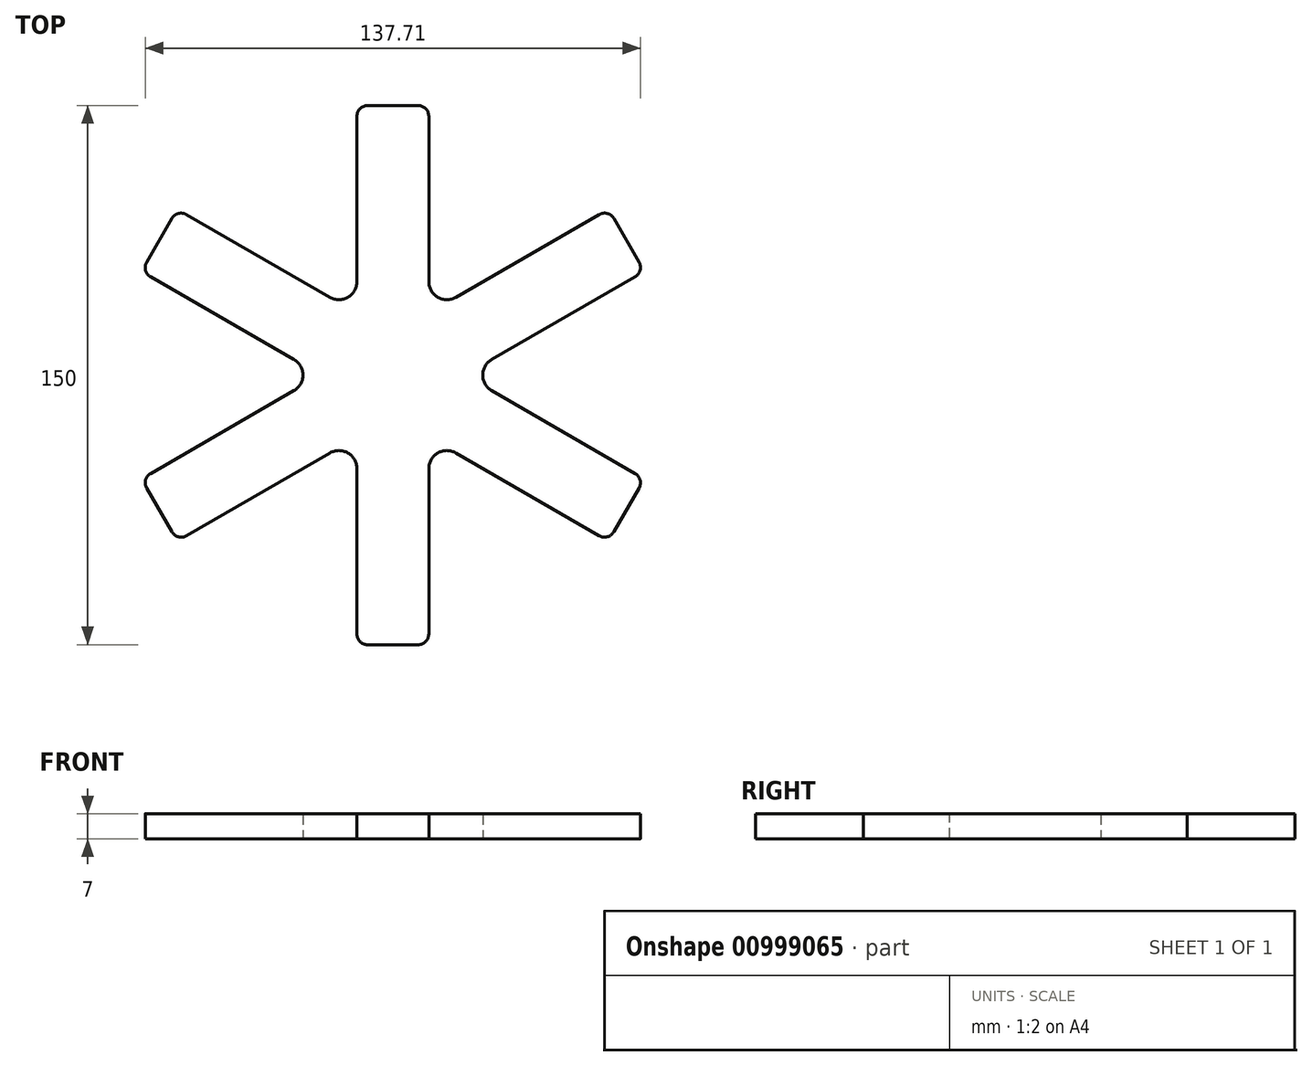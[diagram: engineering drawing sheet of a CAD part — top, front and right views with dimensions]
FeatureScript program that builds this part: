
annotation { "Feature Type Name" : "Feature", "Feature Type Description" : "" }
export const myFeature = defineFeature(function(context is Context, id is Id, definition is map)
    precondition{}
    {
        {
            var Q0;
            Q0=qCreatedBy(makeId("Top.planeOp"),FACE);
            var sketch = newSketch(context, id + "F0", { "sketchPlane" : qUnion([Q0])});
            skLineSegment(sketch, "E0.bottom", {"start": v(-35.4, 96) * mm, "end": v(-15.4, 96) * mm});
            skLineSegment(sketch, "E0.top", {"start": v(-35.4, -54) * mm, "end": v(-15.4, -54) * mm});
            skLineSegment(sketch, "E0.left", {"start": v(-35.4, 96) * mm, "end": v(-35.4, 38.31) * mm});
            skLineSegment(sketch, "E0.right", {"start": v(-15.4, 96) * mm, "end": v(-15.4, 38.31) * mm});
            skLineSegment(sketch, "E1.1.0", {"start": v(44.54, 49.83) * mm, "end": v(-5.4, 21) * mm});
            skLineSegment(sketch, "E1.1.1", {"start": v(34.54, 67.15) * mm, "end": v(44.54, 49.83) * mm});
            skLineSegment(sketch, "E1.1.2", {"start": v(34.54, 67.15) * mm, "end": v(-15.4, 38.31) * mm});
            skLineSegment(sketch, "E1.1.3", {"start": v(-95.36, -7.85) * mm, "end": v(-85.36, -25.17) * mm});
            skLineSegment(sketch, "E1.2.0", {"start": v(34.54, -25.17) * mm, "end": v(-15.4, 3.67) * mm});
            skLineSegment(sketch, "E1.2.1", {"start": v(44.54, -7.85) * mm, "end": v(34.54, -25.17) * mm});
            skLineSegment(sketch, "E1.2.2", {"start": v(44.54, -7.85) * mm, "end": v(-5.4, 21) * mm});
            skLineSegment(sketch, "E1.2.3", {"start": v(-85.36, 67.15) * mm, "end": v(-95.36, 49.83) * mm});
            skPoint(sketch, "E1.center", {"position": v(-25.4, 21) * mm});
            skLineSegment(sketch, "E2.trimOffspring", {"start": v(-45.4, 21) * mm, "end": v(-95.36, -7.85) * mm});
            skLineSegment(sketch, "E3.trimOffspring", {"start": v(-35.4, 3.67) * mm, "end": v(-35.4, -54) * mm});
            skLineSegment(sketch, "E4.trimOffspring", {"start": v(-35.4, 38.31) * mm, "end": v(-85.36, 67.15) * mm});
            skLineSegment(sketch, "E5.trimOffspring", {"start": v(-15.4, 3.67) * mm, "end": v(-15.4, -54) * mm});
            skLineSegment(sketch, "E6.trimOffspring", {"start": v(-45.4, 21) * mm, "end": v(-95.36, 49.83) * mm});
            skLineSegment(sketch, "E7.trimOffspring", {"start": v(-35.4, 3.67) * mm, "end": v(-85.36, -25.17) * mm});
            skSolve(sketch);
        }
        {
            var Q0;
            Q0=makeQuery(id+"F0.imprint","IMPRINT",FACE,{"disambiguationData":[TD([[makeQuery(id+"F0.imprint","IMPRINT",EDGE,{"derivedFrom":sQuery(id+"F0.wireOp",EDGE,"E0.bottom")}),-1.0]])]});
            extrude(context, id + "F1", {"entities" : qUnion([Q0]), "depth" : 7 * mm, "offsetDistance" : 25 * mm});
        }
        {
            var Q0;
            Q0=makeQuery(id+"F1.opExtrude","SWEPT_EDGE",EDGE,{"disambiguationData":[OSD([sQuery(id+"F0.wireOp",EDGE,"E0.top"),sQuery(id+"F0.wireOp",EDGE,"E3.trimOffspring")])]});
            var Q1;
            Q1=makeQuery(id+"F1.opExtrude","SWEPT_EDGE",EDGE,{"disambiguationData":[OSD([sQuery(id+"F0.wireOp",EDGE,"E0.top"),sQuery(id+"F0.wireOp",EDGE,"E5.trimOffspring")])]});
            var Q2;
            Q2=makeQuery(id+"F1.opExtrude","SWEPT_EDGE",EDGE,{"disambiguationData":[OSD([sQuery(id+"F0.wireOp",EDGE,"E1.2.0"),sQuery(id+"F0.wireOp",EDGE,"E1.2.1")])]});
            var Q3;
            Q3=makeQuery(id+"F1.opExtrude","SWEPT_EDGE",EDGE,{"disambiguationData":[OSD([sQuery(id+"F0.wireOp",EDGE,"E1.2.1"),sQuery(id+"F0.wireOp",EDGE,"E1.2.2")])]});
            var Q4;
            Q4=makeQuery(id+"F1.opExtrude","SWEPT_EDGE",EDGE,{"disambiguationData":[OSD([sQuery(id+"F0.wireOp",EDGE,"E1.1.0"),sQuery(id+"F0.wireOp",EDGE,"E1.1.1")])]});
            var Q5;
            Q5=makeQuery(id+"F1.opExtrude","SWEPT_EDGE",EDGE,{"disambiguationData":[OSD([sQuery(id+"F0.wireOp",EDGE,"E1.1.1"),sQuery(id+"F0.wireOp",EDGE,"E1.1.2")])]});
            var Q6;
            Q6=makeQuery(id+"F1.opExtrude","SWEPT_EDGE",EDGE,{"disambiguationData":[OSD([sQuery(id+"F0.wireOp",EDGE,"E1.1.3"),sQuery(id+"F0.wireOp",EDGE,"E7.trimOffspring")])]});
            var Q7;
            Q7=makeQuery(id+"F1.opExtrude","SWEPT_EDGE",EDGE,{"disambiguationData":[OSD([sQuery(id+"F0.wireOp",EDGE,"E1.1.3"),sQuery(id+"F0.wireOp",EDGE,"E2.trimOffspring")])]});
            var Q8;
            Q8=makeQuery(id+"F1.opExtrude","SWEPT_EDGE",EDGE,{"disambiguationData":[OSD([sQuery(id+"F0.wireOp",EDGE,"E1.2.3"),sQuery(id+"F0.wireOp",EDGE,"E4.trimOffspring")])]});
            var Q9;
            Q9=makeQuery(id+"F1.opExtrude","SWEPT_EDGE",EDGE,{"disambiguationData":[OSD([sQuery(id+"F0.wireOp",EDGE,"E1.2.3"),sQuery(id+"F0.wireOp",EDGE,"E6.trimOffspring")])]});
            var Q10;
            Q10=makeQuery(id+"F1.opExtrude","SWEPT_EDGE",EDGE,{"disambiguationData":[OSD([sQuery(id+"F0.wireOp",EDGE,"E0.bottom"),sQuery(id+"F0.wireOp",EDGE,"E0.left")])]});
            fillet(context, id + "F2", {"entities" : qUnion([Q0, Q1, Q2, Q3, Q4, Q5, Q6, Q7, Q8, Q9, Q10]), "radius" : 3 * mm, "tangentPropagation" : true, "allowEdgeOverflow" : false});
        }
        {
            var Q0;
            Q0=makeQuery(id+"F1.opExtrude","SWEPT_EDGE",EDGE,{"disambiguationData":[OSD([sQuery(id+"F0.wireOp",EDGE,"E0.bottom"),sQuery(id+"F0.wireOp",EDGE,"E0.right")])]});
            fillet(context, id + "F3", {"entities" : qUnion([Q0]), "radius" : 3 * mm, "tangentPropagation" : true, "allowEdgeOverflow" : false});
        }
        {
            var Q0;
            Q0=makeQuery(id+"F1.opExtrude","SWEPT_EDGE",EDGE,{"disambiguationData":[OSD([sQuery(id+"F0.wireOp",EDGE,"E0.left"),sQuery(id+"F0.wireOp",EDGE,"E4.trimOffspring")])]});
            var Q1;
            Q1=makeQuery(id+"F1.opExtrude","SWEPT_EDGE",EDGE,{"disambiguationData":[OSD([sQuery(id+"F0.wireOp",EDGE,"E0.right"),sQuery(id+"F0.wireOp",EDGE,"E1.1.2")])]});
            var Q2;
            Q2=makeQuery(id+"F1.opExtrude","SWEPT_EDGE",EDGE,{"disambiguationData":[OSD([sQuery(id+"F0.wireOp",EDGE,"E1.1.0"),sQuery(id+"F0.wireOp",EDGE,"E1.2.2")])]});
            var Q3;
            Q3=makeQuery(id+"F1.opExtrude","SWEPT_EDGE",EDGE,{"disambiguationData":[OSD([sQuery(id+"F0.wireOp",EDGE,"E2.trimOffspring"),sQuery(id+"F0.wireOp",EDGE,"E6.trimOffspring")])]});
            var Q4;
            Q4=makeQuery(id+"F1.opExtrude","SWEPT_EDGE",EDGE,{"disambiguationData":[OSD([sQuery(id+"F0.wireOp",EDGE,"E3.trimOffspring"),sQuery(id+"F0.wireOp",EDGE,"E7.trimOffspring")])]});
            var Q5;
            Q5=makeQuery(id+"F1.opExtrude","SWEPT_EDGE",EDGE,{"disambiguationData":[OSD([sQuery(id+"F0.wireOp",EDGE,"E1.2.0"),sQuery(id+"F0.wireOp",EDGE,"E5.trimOffspring")])]});
            fillet(context, id + "F4", {"entities" : qUnion([Q0, Q1, Q2, Q3, Q4, Q5]), "radius" : 5 * mm, "tangentPropagation" : true, "allowEdgeOverflow" : false});
        }
    });
